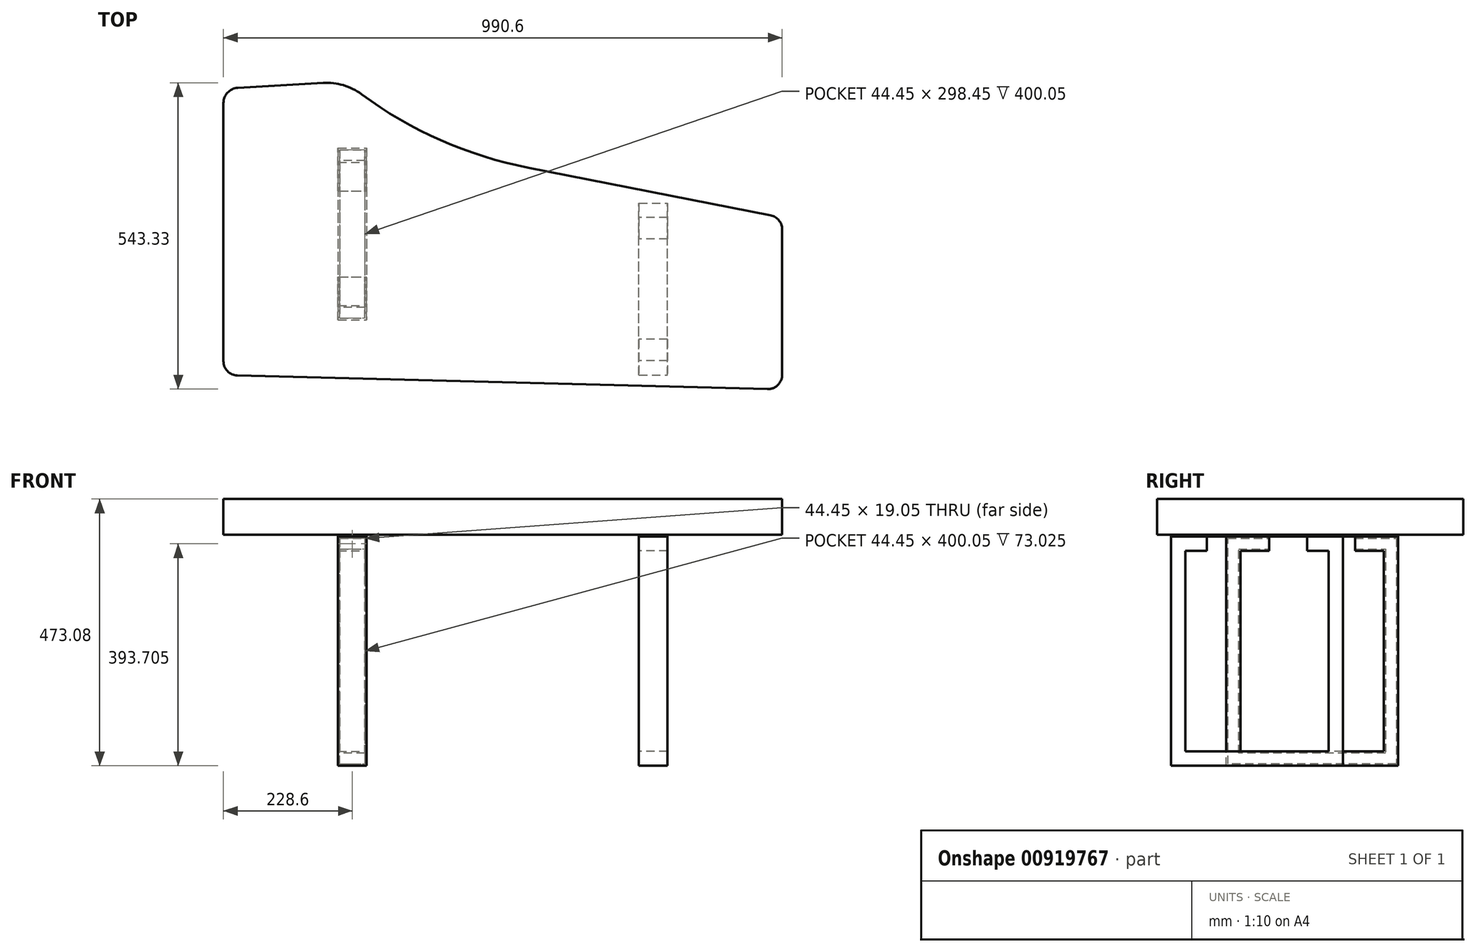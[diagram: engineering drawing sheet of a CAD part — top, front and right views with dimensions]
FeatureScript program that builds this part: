
annotation { "Feature Type Name" : "Feature", "Feature Type Description" : "" }
export const myFeature = defineFeature(function(context is Context, id is Id, definition is map)
    precondition{}
    {
        {
            var Q0;
            Q0=qCreatedBy(makeId("Top.planeOp"),FACE);
            var sketch = newSketch(context, id + "F0", { "sketchPlane" : qUnion([Q0])});
            skLineSegment(sketch, "E0", {"start": v(0, 0) * mm, "end": v(-990.6, 25.4) * mm});
            skLineSegment(sketch, "E1", {"start": v(-990.6, 25.4) * mm, "end": v(-990.6, 533.4) * mm});
            skLineSegment(sketch, "E2", {"start": v(0, 304.8) * mm, "end": v(0, 0) * mm});
            skLineSegment(sketch, "E3", {"start": v(-774.7, 546.1) * mm, "end": v(-990.6, 533.4) * mm});
            skLineSegment(sketch, "E4", {"start": v(-774.7, 546.1) * mm, "end": v(-678.67, 438.15) * mm});
            skLineSegment(sketch, "E5", {"start": v(-678.67, 438.15) * mm, "end": v(0, 304.8) * mm});
            skSolve(sketch);
        }
        {
            var Q0;
            Q0 = qSketchRegion(id + "F0", true);
            extrude(context, id + "F1", {"entities" : qUnion([Q0]), "depth" : 63.5 * mm, "offsetDistance" : 25.4 * mm});
        }
        {
            var Q0;
            Q0=makeQuery(id+"F1.opExtrude","CAP_FACE",FACE,{"disambiguationData":[OSD([sQuery(id+"F0.wireOp",EDGE,"E0"),sQuery(id+"F0.wireOp",EDGE,"E1"),sQuery(id+"F0.wireOp",EDGE,"Xa2x7sSf-Vrwi-sER0-yask-sTqxQ8hoGjD9"),sQuery(id+"F0.wireOp",EDGE,"E2")])],"isStart":true});
            var sketch = newSketch(context, id + "F2", { "sketchPlane" : qUnion([Q0])});
            skLineSegment(sketch, "E6.bottom", {"start": v(-254, -25.39) * mm, "end": v(-203.2, -25.39) * mm});
            skLineSegment(sketch, "E6.top", {"start": v(-254, -330.19) * mm, "end": v(-203.2, -330.19) * mm});
            skLineSegment(sketch, "E6.left", {"start": v(-254, -25.39) * mm, "end": v(-254, -330.19) * mm});
            skLineSegment(sketch, "E6.right", {"start": v(-203.2, -25.39) * mm, "end": v(-203.2, -330.19) * mm});
            skLineSegment(sketch, "E7.bottom", {"start": v(-787.4, -123.28) * mm, "end": v(-736.6, -123.28) * mm});
            skLineSegment(sketch, "E7.top", {"start": v(-787.4, -428.08) * mm, "end": v(-736.6, -428.08) * mm});
            skLineSegment(sketch, "E7.left", {"start": v(-787.4, -123.28) * mm, "end": v(-787.4, -428.08) * mm});
            skLineSegment(sketch, "E7.right", {"start": v(-736.6, -123.28) * mm, "end": v(-736.6, -428.08) * mm});
            skLineSegment(sketch, "E8", {"start": v(-990.6, -25.4) * mm, "end": v(0, 0) * mm, "construction": true});
            skLineSegment(sketch, "E9", {"start": v(0, 0) * mm, "end": v(0, 0) * mm});
            skLineSegment(sketch, "E10", {"start": v(0, 0) * mm, "end": v(-990.6, -25.4) * mm, "construction": true});
            skPoint(sketch, "E11", {"position": v(-254, -177.79) * mm});
            skLineSegment(sketch, "E12", {"start": v(-990.6, -25.4) * mm, "end": v(-990.6, -25.4) * mm});
            skLineSegment(sketch, "E13", {"start": v(0, -152.4) * mm, "end": v(-203.2, -152.4) * mm, "construction": true});
            skLineSegment(sketch, "E14", {"start": v(-787.4, -275.68) * mm, "end": v(-990.6, -275.68) * mm, "construction": true});
            skLineSegment(sketch, "E15", {"start": v(-228.6, -25.39) * mm, "end": v(-228.6, -5.86) * mm, "construction": true});
            skLineSegment(sketch, "E16", {"start": v(-228.6, -330.19) * mm, "end": v(-228.6, -349.72) * mm, "construction": true});
            skLineSegment(sketch, "E17", {"start": v(-762, -428.08) * mm, "end": v(-762, -531.82) * mm, "construction": true});
            skLineSegment(sketch, "E18", {"start": v(-762, -123.28) * mm, "end": v(-762, -19.54) * mm, "construction": true});
            skSolve(sketch);
        }
        {
            var Q0;
            Q0=makeQuery(id+"F1.opExtrude","SWEPT_EDGE",EDGE,{"disambiguationData":[OSD([sQuery(id+"F0.wireOp",EDGE,"E4"),sQuery(id+"F0.wireOp",EDGE,"E5")])]});
            fillet(context, id + "F3", {"entities" : qUnion([Q0]), "radius" : 736.25 * mm, "tangentPropagation" : true, "allowEdgeOverflow" : false});
        }
        {
            var Q0;
            Q0 = qSketchRegion(id + "F2", true);
            extrude(context, id + "F4", {"entities" : qUnion([Q0]), "depth" : 3.17 * mm, "offsetDistance" : 25.4 * mm});
        }
        {
            var Q0;
            Q0=makeQuery(id+"F4.opExtrude","SWEPT_FACE",FACE,{"disambiguationData":[OSD([sQuery(id+"F2.wireOp",EDGE,"E7.left")])]});
            var sketch = newSketch(context, id + "F5", { "sketchPlane" : qUnion([Q0])});
            skLineSegment(sketch, "E19", {"start": v(-123.28, -3.17) * mm, "end": v(-123.28, -409.58) * mm});
            skLineSegment(sketch, "E20", {"start": v(-123.28, -409.58) * mm, "end": v(-428.08, -409.57) * mm});
            skLineSegment(sketch, "E21", {"start": v(-428.08, -409.58) * mm, "end": v(-428.08, -3.17) * mm});
            skLineSegment(sketch, "E22", {"start": v(-428.08, -3.17) * mm, "end": v(-351.88, -3.18) * mm});
            skLineSegment(sketch, "E23", {"start": v(-123.28, -3.18) * mm, "end": v(-199.48, -3.18) * mm});
            skSolve(sketch);
        }
        {
            var Q0;
            Q0=sQuery(id+"F5.wireOp",EDGE,"E22");
            var Q1;
            Q1=sQuery(id+"F5.wireOp",VERTEX,"E22.end");
            cPlane(context, id + "F6", {"entities" : qUnion([Q0, Q1]), "cplaneType" : CPlaneType.LINE_POINT, "offset" : 25.4 * mm, "width" : 152.4 * mm, "height" : 152.4 * mm});
        }
        {
            var Q0;
            Q0=qCreatedBy(id+"F6.planeOp",FACE);
            var sketch = newSketch(context, id + "F7", { "sketchPlane" : qUnion([Q0])});
            skLineSegment(sketch, "E24.bottom", {"start": v(-787.4, -3.17) * mm, "end": v(-736.6, -3.17) * mm});
            skLineSegment(sketch, "E24.top", {"start": v(-787.4, -28.57) * mm, "end": v(-736.6, -28.57) * mm});
            skLineSegment(sketch, "E24.left", {"start": v(-787.4, -3.17) * mm, "end": v(-787.4, -28.57) * mm});
            skLineSegment(sketch, "E24.right", {"start": v(-736.6, -3.18) * mm, "end": v(-736.6, -28.57) * mm});
            skLineSegment(sketch, "E25.0", {"start": v(-784.23, -6.35) * mm, "end": v(-739.78, -6.35) * mm});
            skLineSegment(sketch, "E25.1", {"start": v(-784.23, -6.35) * mm, "end": v(-784.23, -25.4) * mm});
            skLineSegment(sketch, "E25.2", {"start": v(-784.23, -25.4) * mm, "end": v(-739.78, -25.4) * mm});
            skLineSegment(sketch, "E25.3", {"start": v(-739.78, -6.35) * mm, "end": v(-739.78, -25.4) * mm});
            skSolve(sketch);
        }
        {
            var Q0;
            Q0 = qSketchRegion(id + "F7", true);
            var Q1;
            Q1 = qConstructionFilter(qBodyType(qCreatedBy(id + "F5" ,EDGE), BodyType.WIRE), ConstructionObject.NO);
            sweep(context, id + "F8", {"profiles" : qUnion([Q0]), "path" : qUnion([Q1])});
        }
        {
            var Q0;
            Q0=makeQuery(id+"F4.opExtrude","SWEPT_FACE",FACE,{"disambiguationData":[OSD([sQuery(id+"F2.wireOp",EDGE,"E6.right")])]});
            var sketch = newSketch(context, id + "F9", { "sketchPlane" : qUnion([Q0])});
            skLineSegment(sketch, "E26", {"start": v(88.89, -3.18) * mm, "end": v(25.39, -3.18) * mm});
            skLineSegment(sketch, "E27", {"start": v(25.39, -3.17) * mm, "end": v(25.39, -409.57) * mm});
            skLineSegment(sketch, "E28", {"start": v(25.39, -409.57) * mm, "end": v(330.19, -409.57) * mm});
            skLineSegment(sketch, "E29", {"start": v(330.19, -409.57) * mm, "end": v(330.19, -3.17) * mm});
            skLineSegment(sketch, "E30", {"start": v(330.19, -3.18) * mm, "end": v(266.69, -3.18) * mm});
            skSolve(sketch);
        }
        {
            var Q0;
            Q0=sQuery(id+"F9.wireOp",VERTEX,"E26.start");
            var Q1;
            Q1=sQuery(id+"F9.wireOp",EDGE,"E26");
            cPlane(context, id + "F10", {"entities" : qUnion([Q0, Q1]), "cplaneType" : CPlaneType.LINE_POINT, "offset" : 25.4 * mm, "width" : 152.4 * mm, "height" : 152.4 * mm});
        }
        {
            var Q0;
            Q0=qCreatedBy(id+"F10.planeOp",FACE);
            var sketch = newSketch(context, id + "F11", { "sketchPlane" : qUnion([Q0])});
            skLineSegment(sketch, "E31.bottom", {"start": v(-203.2, -3.18) * mm, "end": v(-254, -3.18) * mm});
            skLineSegment(sketch, "E31.top", {"start": v(-203.2, -28.58) * mm, "end": v(-254, -28.58) * mm});
            skLineSegment(sketch, "E31.left", {"start": v(-203.2, -3.18) * mm, "end": v(-203.2, -28.57) * mm});
            skLineSegment(sketch, "E31.right", {"start": v(-254, -3.18) * mm, "end": v(-254, -28.58) * mm});
            skSolve(sketch);
        }
        {
            var Q0;
            Q0 = qSketchRegion(id + "F11", true);
            var Q1;
            Q1 = qConstructionFilter(qBodyType(qCreatedBy(id + "F9" ,EDGE), BodyType.WIRE), ConstructionObject.NO);
            sweep(context, id + "F12", {"profiles" : qUnion([Q0]), "path" : qUnion([Q1])});
        }
        {
            var Q0;
            Q0=makeQuery(id+"F3.opFillet","BLEND_EDGE",EDGE,{"blendedFrom":[makeQuery(id+"F1.opExtrude","SWEPT_EDGE",EDGE,{"disambiguationData":[OSD([sQuery(id+"F0.wireOp",EDGE,"E4"),sQuery(id+"F0.wireOp",EDGE,"E5")])]}),makeQuery(id+"F1.opExtrude","SWEPT_FACE",FACE,{"disambiguationData":[OSD([sQuery(id+"F0.wireOp",EDGE,"E3")])]})],"blendedInto":[makeQuery(id+"F1.opExtrude","SWEPT_FACE",FACE,{"disambiguationData":[OSD([sQuery(id+"F0.wireOp",EDGE,"E3")])]})]});
            fillet(context, id + "F13", {"entities" : qUnion([Q0]), "radius" : 103.49 * mm, "tangentPropagation" : true, "allowEdgeOverflow" : false});
        }
        {
            var Q0;
            Q0=makeQuery(id+"F1.opExtrude","SWEPT_EDGE",EDGE,{"disambiguationData":[OSD([sQuery(id+"F0.wireOp",EDGE,"E1"),sQuery(id+"F0.wireOp",EDGE,"E3")])]});
            fillet(context, id + "F14", {"entities" : qUnion([Q0]), "radius" : 27.13 * mm, "tangentPropagation" : true, "allowEdgeOverflow" : false});
        }
        {
            var Q0;
            Q0=makeQuery(id+"F1.opExtrude","SWEPT_EDGE",EDGE,{"disambiguationData":[OSD([sQuery(id+"F0.wireOp",EDGE,"E0"),sQuery(id+"F0.wireOp",EDGE,"E1")])]});
            var Q1;
            Q1=makeQuery(id+"F1.opExtrude","SWEPT_EDGE",EDGE,{"disambiguationData":[OSD([sQuery(id+"F0.wireOp",EDGE,"E0"),sQuery(id+"F0.wireOp",EDGE,"E2")])]});
            var Q2;
            Q2=makeQuery(id+"F1.opExtrude","SWEPT_EDGE",EDGE,{"disambiguationData":[OSD([sQuery(id+"F0.wireOp",EDGE,"E2"),sQuery(id+"F0.wireOp",EDGE,"E5")])]});
            fillet(context, id + "F15", {"entities" : qUnion([Q0, Q1, Q2]), "radius" : 25.4 * mm, "tangentPropagation" : true, "allowEdgeOverflow" : false});
        }
    });
